# Revit family: ASH_Contour21_S0440_BIM_GB
name_source: partatom
category: Plumbing Fixtures
revit_build: Autodesk Revit MEP 2014 (Build: 20130308_1515(x64)
units: mm (PartAtom-declared; Revit-internal decimal feet)

## types (1)
- S0440HY - Contour 21+ Back-to wall rimless WC bowl - Raised height - hygenic+ glaze
    Accessories = www.idealspec.co.uk
    AreaUnits = millimeters
    Assembly Code = C1030200
    AssetType = Fixed
    BIMObjectName = ASH_AmitageShanks_WCPans_Contour 21+_S0440HY
    BREEAMApproved = No
    Brand = Armitage Shanks
    CWFU = 0
    ConnectionType = Plumbing
    Cost = 0 $
    Default Elevation = 450 mm  [stored 1.47638 ft]
    Description = Contour 21+ back to wall rimless raised height wc pan standard projection  anti-bacterial glaze
    DurationUnit = year
    ECA = No
    ExpectedLife = 30
    Features = Back to wall rimless raised height wc pan standard projection  anti-bacterial glaze
    Finish = White
    HWFU = 0
    Help = www.idealspec.co.uk/contact-us.html
    IfcExportAs = IfcSanitaryTerminalType
    IfcExportType = TOILETPAN
    InstallationInstructions = www.idealspec.co.uk/resources.html
    LinearUnits = millimeters
    ManufacturerURL = www.idealspec.co.uk
    Model = S0440HY
    ModelNumber = S0440HY
    ModelReference = Contour 21+ back to wall rimless raised height wc pan standard projection  anti-bacterial glaze
    NBSDescription = WC pans
    NBSReference = 45-30-70/384
    Name = WCPans_Contour 21+_S0440HY_AmitageShanks
    NettWeight = 22.7 kg
    NominalDepth = 520 mm  [stored 1.70604 ft]
    NominalHeight = 450 mm  [stored 1.47638 ft]
    NominalLength = 360 mm
    NominalWidth = 360 mm
    PanColor = White
    PanMaterial = Vitreous china
    PanMounting = BackToWall
    ProductInformation = www.idealspec.co.uk
    Shape = Sculptured
    Size = 520 x 360 x 450 mm
    Space = Internal
    SpilloverLevel = 0 mm  [stored 0 ft]
    ToiletPanType = WashDown
    ToiletType = Other
    URL = www.idealspec.co.uk
    Uniclass2015Code = Pr_40_20_93_94
    Uniclass2015Title = WC pans
    Uniclass2015Version = Products v1.1
    Version = 1
    VolumeUnits = Litres
    WFU = 0
    WRAS = No
    WarrantyDescription = Manufacturers Warranty
    WarrantyDurationParts = 99
    WarrantyDurationUnit = year
    WaterEfficientProduct = No

note: [stored X ft] marks values corroborated as IEEE doubles in the binary element streams (Revit-internal decimal feet)

## geometry (parser evidence)
native form markers: Sweep x2
no freeform markers — native parametric forms only
